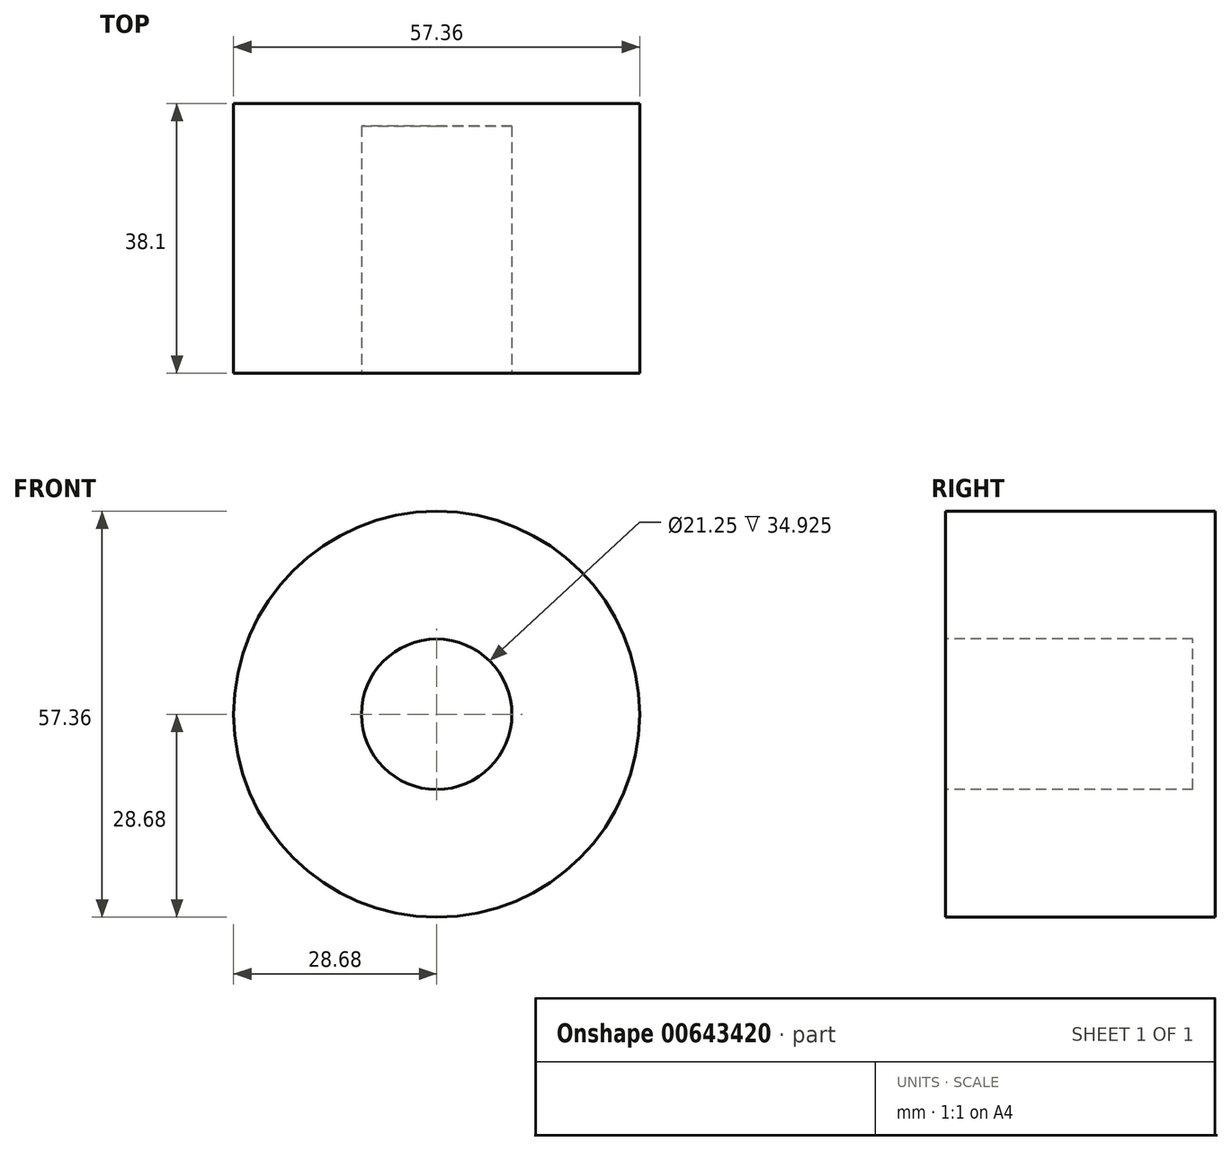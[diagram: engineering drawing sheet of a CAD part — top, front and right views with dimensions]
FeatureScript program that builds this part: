
annotation { "Feature Type Name" : "Feature", "Feature Type Description" : "" }
export const myFeature = defineFeature(function(context is Context, id is Id, definition is map)
    precondition{}
    {
        {
            var Q0;
            Q0=qCreatedBy(makeId("Front.planeOp"),FACE);
            var sketch = newSketch(context, id + "F0", { "sketchPlane" : qUnion([Q0])});
            skCircle(sketch, "E0", {"center": v(0, 0) * mm, "radius": 28.68 * mm});
            skSolve(sketch);
        }
        {
            var Q0;
            Q0=makeQuery(id+"F0.imprint","IMPRINT",FACE,{"disambiguationData":[TD([[makeQuery(id+"F0.imprint","IMPRINT",EDGE,{"derivedFrom":sQuery(id+"F0.wireOp",EDGE,"E0")}),1.0]])]});
            extrude(context, id + "F1", {"entities" : qUnion([Q0]), "depth" : 38.1 * mm, "offsetDistance" : 25.4 * mm});
        }
        {
            var Q0;
            Q0=makeQuery(id+"F1.opExtrude","CAP_FACE",FACE,{"disambiguationData":[OSD([sQuery(id+"F0.wireOp",EDGE,"E0")])],"isStart":false});
            var sketch = newSketch(context, id + "F2", { "sketchPlane" : qUnion([Q0])});
            skCircle(sketch, "E1", {"center": v(0, 0) * mm, "radius": 10.62 * mm});
            skCircle(sketch, "E2", {"center": v(0, 0) * mm, "radius": 8.96 * mm});
            skSolve(sketch);
        }
        {
            var Q0;
            Q0 = qSketchRegion(id + "F2", true);
            var Q1;
            Q1=makeQuery(id+"F2.imprint","IMPRINT",FACE,{"disambiguationData":[TD([[makeQuery(id+"F2.imprint","IMPRINT",EDGE,{"derivedFrom":sQuery(id+"F2.wireOp",EDGE,"E2")}),1.0]])]});
            extrude(context, id + "F3", {"entities" : qUnion([Q0, Q1]), "operationType" : NewBodyOperationType.REMOVE, "oppositeDirection" : true, "depth" : 34.92 * mm, "offsetDistance" : 25.4 * mm});
        }
    });
